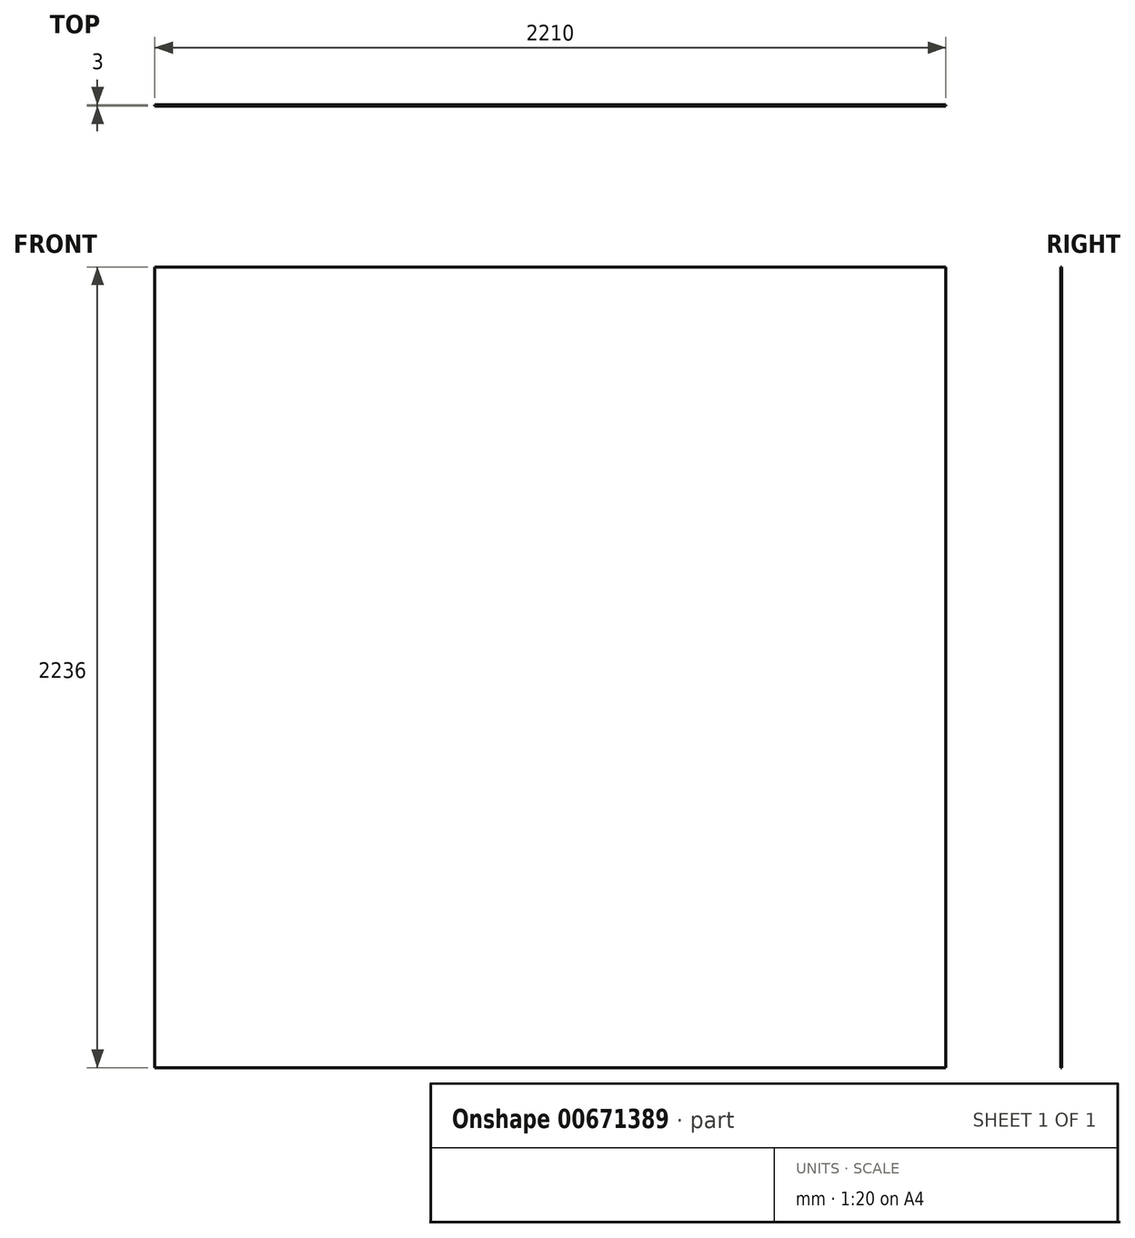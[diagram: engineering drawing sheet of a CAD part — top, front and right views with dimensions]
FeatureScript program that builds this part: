
annotation { "Feature Type Name" : "Feature", "Feature Type Description" : "" }
export const myFeature = defineFeature(function(context is Context, id is Id, definition is map)
    precondition{}
    {
        {
            var Q0;
            Q0=qCreatedBy(makeId("Front.planeOp"),FACE);
            var sketch = newSketch(context, id + "F0", { "sketchPlane" : qUnion([Q0])});
            skLineSegment(sketch, "E0.bottom", {"start": v(-1102.57, 1473.35) * mm, "end": v(1107.43, 1473.35) * mm});
            skLineSegment(sketch, "E0.top", {"start": v(-1102.57, -762.65) * mm, "end": v(1107.43, -762.65) * mm});
            skLineSegment(sketch, "E0.left", {"start": v(-1102.57, 1473.35) * mm, "end": v(-1102.57, -762.65) * mm});
            skLineSegment(sketch, "E0.right", {"start": v(1107.43, 1473.35) * mm, "end": v(1107.43, -762.65) * mm});
            skSolve(sketch);
        }
        {
            var Q0;
            Q0=qSketchRegion(id+"F0",true);
            extrude(context, id + "F1", {"entities" : qUnion([Q0]), "endBound" : BoundingType.SYMMETRIC, "depth" : 3 * mm, "offsetDistance" : 25 * mm});
        }
    });
